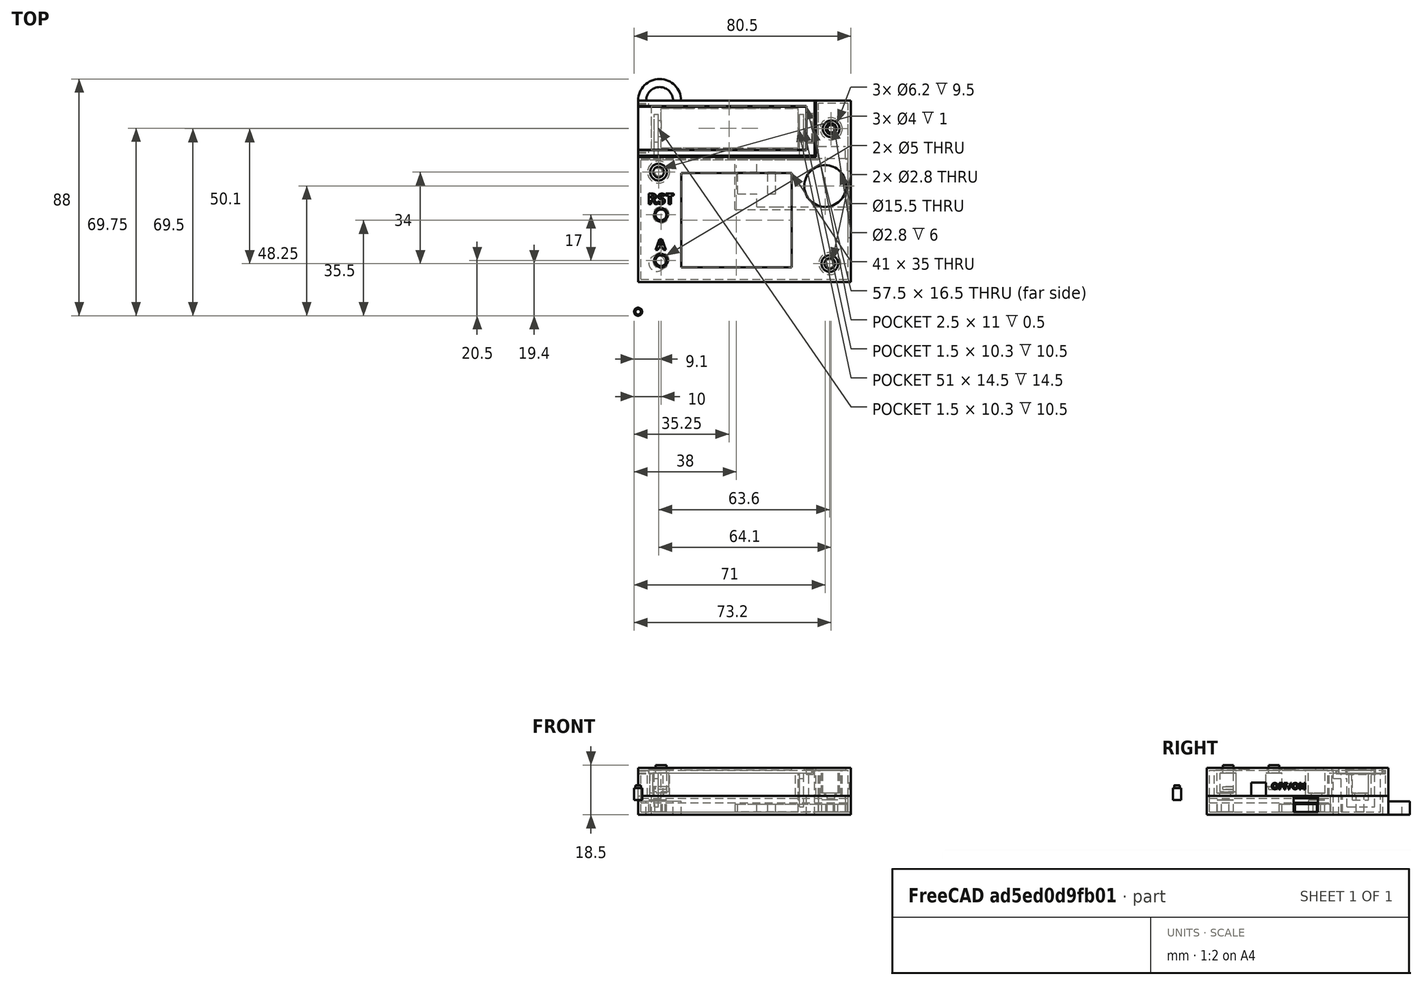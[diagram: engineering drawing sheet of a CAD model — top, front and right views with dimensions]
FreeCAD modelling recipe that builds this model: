
FCSTD DOCUMENT  (FreeCAD 0.18R16131 (Git))
Label: magic_8_power
License: All rights reserved
LicenseURL: http://en.wikipedia.org/wiki/All_rights_reserved
objects: Part::Cut×44, Part::Box×39, Part::Cylinder×28, Part::MultiFuse×10, Part::Part2DObjectPython×3, Part::Extrusion×3
note: 127 computed .brp shape members not serialized (recipe doc carries the construction recipe); baked Part::Feature solids carry a one-line shape summary decoded from their .brp

FEATURE [Part::Box] Box008  label="Cube003(usb_C_charger)"
  AttacherType = Attacher::AttachEngine3D
  Height = 3
  Length = 26.7
  Placement = pos=(27.1,-19,0) rot=(0,0,1;0rad)
  Width = 17.7
FEATURE [Part::Box] Box011  label="Cube(big_base)"
  AttacherType = Attacher::AttachEngine3D
  Height = 4
  Length = 43
  Placement = pos=(12,-20,-1) rot=(0,0,1;0rad)
  Width = 20
FEATURE [Part::Box] Box012  label="Cube(usb_c_gap)"
  AttacherType = Attacher::AttachEngine3D
  Height = 3
  Length = 3
  Placement = pos=(53.8,-14.65,0) rot=(0,0,1;0rad)
  Width = 9
FEATURE [Part::Box] Box013  label="Cube(wire_gap)"
  AttacherType = Attacher::AttachEngine3D
  Height = 3
  Length = 7
  Placement = pos=(20.1,-6.1,0) rot=(0,0,1;0rad)
  Width = 4.8
FEATURE [Part::Box] Box007  label="Cube002(DC_DC_boost)"
  AttacherType = Attacher::AttachEngine3D
  Height = 3
  Length = 11.2
  Placement = pos=(13,-14.2,0) rot=(0,0,1;0rad)
  Width = 8.1
FEATURE [Part::Box] Box014  label="Cube(wire_gap)001"
  AttacherType = Attacher::AttachEngine3D
  Height = 3
  Length = 7
  Placement = pos=(20.1,-19,0) rot=(0,0,1;0rad)
  Width = 4.8
FEATURE [Part::Cut] Cut023
  Base = -> Box011
  Tool = -> Box012
FEATURE [Part::Cut] Cut024
  Base = -> Cut023
  Tool = -> Box014
FEATURE [Part::Cut] Cut025
  Base = -> Cut024
  Tool = -> Box013
FEATURE [Part::Cut] Cut026
  Base = -> Cut025
  Tool = -> Box007
FEATURE [Part::Cut] Cut027  label="Cut027(power_board)"
  Base = -> Cut026
  Placement = pos=(24,-2,-4.5) rot=(0,0,1;0rad)
  Tool = -> Box008
FEATURE [Part::Box] Box032  label="Cube(pcb_inner)"
  AttacherType = Attacher::AttachEngine3D
  Height = 1.6
  Length = 77
  Placement = pos=(1,-48,-1) rot=(0,0,1;0rad)
  Width = 45
FEATURE [Part::Cylinder] Cylinder002  label="Cylinder(screw_left_inner)"
  Angle = 360
  AttacherType = Attacher::AttachEngine3D
  Height = 4.5
  Placement = pos=(7.6,-8.1,-4.5) rot=(0,0,1;0rad)
  Radius = 1.4
FEATURE [Part::Cylinder] Cylinder003  label="Cylinder(screw_right_inner)"
  Angle = 360
  AttacherType = Attacher::AttachEngine3D
  Height = 4.5
  Placement = pos=(71.2,-42.1,-4.5) rot=(0,0,1;0rad)
  Radius = 1.4
FEATURE [Part::Box] Box  label="Cube(inner_box)"
  AttacherType = Attacher::AttachEngine3D
  Height = 17.5
  Length = 57.5
  Placement = pos=(5,0,-5.5) rot=(0,0,1;0rad)
  Width = 16.5
FEATURE [Part::Box] Box002  label="Cube002(cover_end_gap)"
  AttacherType = Attacher::AttachEngine3D
  Height = 1.25
  Length = 4
  Placement = pos=(0,-1,9.75) rot=(0,0,1;0rad)
  Width = 18.5
FEATURE [Part::Box] Box003  label="Cube003(cover_end_top_gap)"
  AttacherType = Attacher::AttachEngine3D
  Height = 1
  Length = 5
  Placement = pos=(0,0,11) rot=(0,0,1;0rad)
  Width = 16.5
FEATURE [Part::Box] Box004  label="Cube004(lid_inner_lip)"
  AttacherType = Attacher::AttachEngine3D
  Height = 0.75
  Length = 4
  Placement = pos=(0,-0.75,10) rot=(0,0,1;0rad)
  Width = 18
FEATURE [Part::Box] Box005  label="Cube005(lid)"
  AttacherType = Attacher::AttachEngine3D
  Height = 2
  Length = 62.5
  Placement = pos=(0,0.25,10) rot=(0,0,1;0rad)
  Width = 16
FEATURE [Part::Box] Box006  label="Cube004"
  AttacherType = Attacher::AttachEngine3D
  Height = 14.5
  Length = 51
  Placement = pos=(1,1,0) rot=(0,0,1;0rad)
  Width = 14.5
FEATURE [Part::Box] Box033  label="Cube005"
  AttacherType = Attacher::AttachEngine3D
  Height = 15.5
  Length = 57.5
  Placement = pos=(-2.5,0,-1) rot=(0,0,1;0rad)
  Width = 16.5
FEATURE [Part::Box] Box034  label="Cube002(minus_spring)"
  AttacherType = Attacher::AttachEngine3D
  Height = 12.5
  Length = 1.5
  Placement = pos=(-1.5,3.1,2) rot=(0,0,1;0rad)
  Width = 10.3
FEATURE [Part::Box] Box009  label="Cube003(plus_end)"
  AttacherType = Attacher::AttachEngine3D
  Height = 12.5
  Length = 1.5
  Placement = pos=(52.5,3.1,2) rot=(0,0,1;0rad)
  Width = 10.3
FEATURE [Part::Box] Box010  label="Cube002(minus_spring_gap)"
  AttacherType = Attacher::AttachEngine3D
  Height = 10
  Length = 5
  Placement = pos=(0,5.1,4.5) rot=(0,0,1;0rad)
  Width = 6
FEATURE [Part::Box] Box035  label="Cube003(plus_end_gap)"
  AttacherType = Attacher::AttachEngine3D
  Height = 10
  Length = 5
  Placement = pos=(47.5,5.1,4.5) rot=(0,0,1;0rad)
  Width = 6
FEATURE [Part::Cut] Cut002
  Base = -> Box033
  Tool = -> Box006
FEATURE [Part::Cut] Cut003
  Base = -> Cut002
  Tool = -> Box034
FEATURE [Part::Cut] Cut004
  Base = -> Cut003
  Tool = -> Box009
FEATURE [Part::Cut] Cut005
  Base = -> Cut004
  Tool = -> Box010
FEATURE [Part::Cut] Cut006
  Base = -> Cut005
  Placement = pos=(7.5,0,-4.5) rot=(0,0,1;0rad)
  Tool = -> Box035
FEATURE [Part::Box] Box036  label="Cube006(outer_box)"
  AttacherType = Attacher::AttachEngine3D
  Height = 17.5
  Length = 60.5
  Placement = pos=(5,-2,-5.5) rot=(0,0,1;0rad)
  Width = 20.5
FEATURE [Part::Box] Box037  label="Cube007(tange_inner)"
  AttacherType = Attacher::AttachEngine3D
  Height = 1
  Length = 2
  Placement = pos=(62.5,3.25,10) rot=(0,0,1;0rad)
  Width = 10
FEATURE [Part::Box] Box038  label="Cube007(tange_outer)"
  AttacherType = Attacher::AttachEngine3D
  Height = 2
  Length = 2.5
  Placement = pos=(62.5,2.75,9.5) rot=(0,0,1;0rad)
  Width = 11
FEATURE [Part::Box] Box015  label="Cube006(under_cover_end)"
  AttacherType = Attacher::AttachEngine3D
  Height = 17.5
  Length = 5
  Placement = pos=(0,-2,-5.5) rot=(0,0,1;0rad)
  Width = 20.5
FEATURE [Part::Cut] Cut
  Base = -> Box036
  Tool = -> Box
FEATURE [Part::Cut] Cut010
  Base = -> Cut
  Tool = -> Box038
FEATURE [Part::Cut] Cut011
  Base = -> Box015
  Tool = -> Box003
FEATURE [Part::Box] Box016  label="Cube002(cover_end_gap_middle)"
  AttacherType = Attacher::AttachEngine3D
  Height = 1.25
  Length = 5
  Placement = pos=(0,0,9.75) rot=(0,0,1;0rad)
  Width = 16.5
FEATURE [Part::Cut] Cut012
  Base = -> Cut011
  Tool = -> Box016
FEATURE [Part::Cut] Cut013
  Base = -> Cut012
  Tool = -> Box002
FEATURE [Part::MultiFuse] Fusion  label="Fusion(battery_lid)"
  Shapes = -> [Box004,Box005,Box037]
FEATURE [Part::MultiFuse] Fusion001
  Shapes = -> [Cut006,Cut013,Cut010]
FEATURE [Part::Box] Box039  label="Cube(outer_case)"
  AttacherType = Attacher::AttachEngine3D
  Height = 7
  Length = 79
  Placement = pos=(0,-49,-5.5) rot=(0,0,1;0rad)
  Width = 67.5
FEATURE [Part::Cylinder] Cylinder004  label="Cylinder(screw_left_outer)"
  Angle = 360
  AttacherType = Attacher::AttachEngine3D
  Height = 4.5
  Placement = pos=(7.6,-8.1,-4.5) rot=(0,0,1;0rad)
  Radius = 3
FEATURE [Part::Cylinder] Cylinder005  label="Cylinder(screw_right_outer)"
  Angle = 360
  AttacherType = Attacher::AttachEngine3D
  Height = 4.5
  Placement = pos=(71.2,-42.1,-4.5) rot=(0,0,1;0rad)
  Radius = 3
FEATURE [Part::Box] Box040  label="Cube(gnd_wire)"
  AttacherType = Attacher::AttachEngine3D
  Height = 2
  Length = 1.5
  Placement = pos=(6,-2,8) rot=(0,0,1;0rad)
  Width = 6
FEATURE [Part::Box] Box041  label="Cube(vcc_wire)"
  AttacherType = Attacher::AttachEngine3D
  Height = 2
  Length = 1.5
  Placement = pos=(60,-2,8) rot=(0,0,1;0rad)
  Width = 6
FEATURE [Part::Box] Box042  label="Cube(switch_gap)"
  AttacherType = Attacher::AttachEngine3D
  Height = 5
  Length = 2
  Placement = pos=(78,-32.5,1.5) rot=(0,0,1;0rad)
  Width = 5.5
FEATURE [Part::Box] Box043  label="Cube(pcb_space)"
  AttacherType = Attacher::AttachEngine3D
  Height = 6
  Length = 77
  Placement = pos=(1,-48,-4.5) rot=(0,0,1;0rad)
  Width = 45
FEATURE [Part::Cylinder] Cylinder  label="Cylinder(3rd screw_inner)"
  Angle = 360
  AttacherType = Attacher::AttachEngine3D
  Height = 6
  Placement = pos=(71.7,8,-4.5) rot=(0,0,1;0rad)
  Radius = 1.4
FEATURE [Part::Box] Box044  label="Cube(battery_space)"
  AttacherType = Attacher::AttachEngine3D
  Height = 17.5
  Length = 57.5
  Placement = pos=(5,0,-5.5) rot=(0,0,1;0rad)
  Width = 16.5
FEATURE [Part::Box] Box046  label="Cube(mirco_usb_port)"
  AttacherType = Attacher::AttachEngine3D
  Height = 6
  Length = 1.2
  Placement = pos=(77.8,-16.65,-4.5) rot=(0,0,1;0rad)
  Width = 9
FEATURE [Part::Box] Box047  label="Cube(outer_lid)"
  AttacherType = Attacher::AttachEngine3D
  Height = 10.5
  Length = 79
  Placement = pos=(0,-49,1.5) rot=(0,0,1;0rad)
  Width = 46.5
FEATURE [Part::Box] Box048  label="Cube(inner_lid)"
  AttacherType = Attacher::AttachEngine3D
  Height = 9.5
  Length = 77
  Placement = pos=(1,-48,1.5) rot=(0,0,1;0rad)
  Width = 44.5
FEATURE [Part::Box] Box049  label="Cube(3rd_screw_cover_outer)"
  AttacherType = Attacher::AttachEngine3D
  Height = 10.5
  Length = 13
  Placement = pos=(66,-2.5,1.5) rot=(0,0,1;0rad)
  Width = 21
FEATURE [Part::Cylinder] Cylinder006  label="Cylinder(3rd screw_lid_clear)"
  Angle = 360
  AttacherType = Attacher::AttachEngine3D
  Height = 10.5
  Placement = pos=(71.7,8,0.5) rot=(0,0,1;0rad)
  Radius = 2
FEATURE [Part::Cylinder] Cylinder007  label="Cylinder(3rd screw_lid_head_clear_inner)"
  Angle = 360
  AttacherType = Attacher::AttachEngine3D
  Height = 9.5
  Placement = pos=(71.7,8,2.5) rot=(0,0,1;0rad)
  Radius = 3.1
FEATURE [Part::Box] Box050  label="Cube(3rd_screw_cover_inner)"
  AttacherType = Attacher::AttachEngine3D
  Height = 10.5
  Length = 11
  Placement = pos=(67,-3.5,0.5) rot=(0,0,1;0rad)
  Width = 21
FEATURE [Part::Cylinder] Cylinder008  label="Cylinder(3rd screw_lid_head_clear_outer)"
  Angle = 360
  AttacherType = Attacher::AttachEngine3D
  Height = 10.5
  Placement = pos=(71.7,8,1.5) rot=(0,0,1;0rad)
  Radius = 4.1
FEATURE [Part::Cut] Cut030
  Base = -> Fusion001
  Tool = -> Box040
FEATURE [Part::Cut] Cut031  label="Cut031(battery)"
  Base = -> Cut030
  Tool = -> Box041
FEATURE [Part::Cylinder] Cylinder009  label="Cylinder(gx-12_hole)"
  Angle = 360
  AttacherType = Attacher::AttachEngine3D
  Height = 10
  Placement = pos=(69.5,-13.25,3) rot=(0,0,1;0rad)
  Radius = 7.75
FEATURE [Part::Box] Box051  label="Cube(screen_cutout)"
  AttacherType = Attacher::AttachEngine3D
  Height = 10
  Length = 41
  Placement = pos=(16,-43.5,3) rot=(0,0,1;0rad)
  Width = 35
FEATURE [Part::Cut] Cut032
  Base = -> Box039
  Tool = -> Box043
FEATURE [Part::Cut] Cut033
  Base = -> Cut032
  Tool = -> Box044
FEATURE [Part::Cut] Cut034
  Base = -> Cut033
  Tool = -> Cylinder
FEATURE [Part::Cut] Cut037
  Base = -> Cut034
  Tool = -> Box046
FEATURE [Part::Cylinder] Cylinder011  label="Cylinder(under_button_post)"
  Angle = 360
  AttacherType = Attacher::AttachEngine3D
  Height = 4.5
  Placement = pos=(7,-42,-4.5) rot=(0,0,1;0rad)
  Radius = 3
FEATURE [Part::Cylinder] Cylinder012  label="Cylinder(lanyard_outer)"
  Angle = 360
  AttacherType = Attacher::AttachEngine3D
  Height = 5
  Placement = pos=(8,18.5,-5.5) rot=(0,0,1;0rad)
  Radius = 8
FEATURE [Part::Cylinder] Cylinder013  label="Cylinder(lanyard_inner)"
  Angle = 360
  AttacherType = Attacher::AttachEngine3D
  Height = 5
  Placement = pos=(8,18.5,-5.5) rot=(0,0,1;0rad)
  Radius = 5
FEATURE [Part::Box] Box052  label="Cube(lanyard_cut)"
  AttacherType = Attacher::AttachEngine3D
  Height = 10
  Length = 16
  Placement = pos=(0,8.5,-5.5) rot=(0,0,1;0rad)
  Width = 10
FEATURE [Part::Cut] Cut038
  Base = -> Cylinder012
  Tool = -> Cylinder013
FEATURE [Part::Cut] Cut039  label="Cut039(lanyard)"
  Base = -> Cut038
  Tool = -> Box052
FEATURE [Part::Box] Box053  label="Cube(cable_gap)"
  AttacherType = Attacher::AttachEngine3D
  Height = 6
  Length = 10
  Placement = pos=(67,-3.5,-4.5) rot=(0,0,1;0rad)
  Width = 5
FEATURE [Part::MultiFuse] Fusion002
  Shapes = -> [Cut037,Cut027]
FEATURE [Part::Cut] Cut040
  Base = -> Fusion002
  Tool = -> Box053
FEATURE [Part::Cylinder] Cylinder014  label="Cylinder(screw_left_lid_clear)"
  Angle = 360
  AttacherType = Attacher::AttachEngine3D
  Height = 10.5
  Placement = pos=(7.6,-8.1,0.5) rot=(0,0,1;0rad)
  Radius = 2
FEATURE [Part::Cylinder] Cylinder015  label="Cylinder(screw_left_head_clear_inner)"
  Angle = 360
  AttacherType = Attacher::AttachEngine3D
  Height = 9.5
  Placement = pos=(7.6,-8.1,2.5) rot=(0,0,1;0rad)
  Radius = 3.1
FEATURE [Part::Cylinder] Cylinder016  label="Cylinder(screw_left_head_clear_outer)"
  Angle = 360
  AttacherType = Attacher::AttachEngine3D
  Height = 10.5
  Placement = pos=(7.6,-8.1,1.5) rot=(0,0,1;0rad)
  Radius = 4.1
FEATURE [Part::Cut] Cut041
  Base = -> Cylinder004
  Tool = -> Cylinder002
FEATURE [Part::Cylinder] Cylinder017  label="Cylinder(screw_right_lid_clear)"
  Angle = 360
  AttacherType = Attacher::AttachEngine3D
  Height = 10.5
  Placement = pos=(71.2,-42.1,0.5) rot=(0,0,1;0rad)
  Radius = 2
FEATURE [Part::Cut] Cut042
  Base = -> Cylinder005
  Tool = -> Cylinder003
FEATURE [Part::Cylinder] Cylinder018  label="Cylinder(screw_right_head_clear_inner)"
  Angle = 360
  AttacherType = Attacher::AttachEngine3D
  Height = 9.5
  Placement = pos=(71.2,-42.1,2.5) rot=(0,0,1;0rad)
  Radius = 3.1
FEATURE [Part::Cylinder] Cylinder019  label="Cylinder(screw_right_head_clear_outer)"
  Angle = 360
  AttacherType = Attacher::AttachEngine3D
  Height = 10.5
  Placement = pos=(71.2,-42.1,1.5) rot=(0,0,1;0rad)
  Radius = 4.1
FEATURE [Part::Box] Box054  label="Cube(GND_wire_cover_hole)"
  AttacherType = Attacher::AttachEngine3D
  Height = 8.5
  Length = 5
  Placement = pos=(4.3,-3.5,1.5) rot=(0,0,1;0rad)
  Width = 1
FEATURE [Part::Box] Box055  label="Cube(VCC_wire_cover_hole)"
  AttacherType = Attacher::AttachEngine3D
  Height = 8.5
  Length = 5
  Placement = pos=(58.4,-3.5,1.5) rot=(0,0,1;0rad)
  Width = 1
FEATURE [Part::Cylinder] Cylinder020  label="Cylinder(reset_button_hole)"
  Angle = 360
  AttacherType = Attacher::AttachEngine3D
  Height = 10
  Placement = pos=(8.5,-24,3) rot=(0,0,1;0rad)
  Radius = 2.5
FEATURE [Part::Cylinder] Cylinder021  label="Cylinder(a_button_hole)"
  Angle = 360
  AttacherType = Attacher::AttachEngine3D
  Height = 10
  Placement = pos=(8.5,-41,3) rot=(0,0,1;0rad)
  Radius = 2.5
FEATURE [Part::MultiFuse] Fusion003
  Shapes = -> [Box047,Box049]
FEATURE [Part::Cut] Cut043
  Base = -> Fusion003
  Tool = -> Box048
FEATURE [Part::Cut] Cut044
  Base = -> Cut043
  Tool = -> Box050
FEATURE [Part::Cut] Cut045
  Base = -> Cut044
  Tool = -> Box055
FEATURE [Part::Cut] Cut046
  Base = -> Cut045
  Tool = -> Box054
FEATURE [Part::MultiFuse] Fusion004
  Shapes = -> [Cylinder019,Cut046]
FEATURE [Part::MultiFuse] Fusion005
  Shapes = -> [Fusion004,Cylinder016]
FEATURE [Part::Cut] Cut047
  Base = -> Fusion005
  Tool = -> Cylinder018
FEATURE [Part::Cut] Cut048
  Base = -> Cut047
  Tool = -> Cylinder017
FEATURE [Part::Cut] Cut049
  Base = -> Cut048
  Tool = -> Cylinder014
FEATURE [Part::Cut] Cut050
  Base = -> Cut049
  Tool = -> Cylinder015
FEATURE [Part::Cut] Cut051
  Base = -> Cut050
  Tool = -> Cylinder021
FEATURE [Part::Cut] Cut052
  Base = -> Cut051
  Tool = -> Cylinder020
FEATURE [Part::Cut] Cut053
  Base = -> Cut052
  Tool = -> Box051
FEATURE [Part::Cut] Cut054
  Base = -> Cut053
  Tool = -> Cylinder009
FEATURE [Part::MultiFuse] Fusion006
  Shapes = -> [Cut054,Cylinder008]
FEATURE [Part::Cut] Cut055
  Base = -> Fusion006
  Tool = -> Cylinder006
FEATURE [Part::Cut] Cut056
  Base = -> Cut055
  Tool = -> Cylinder007
FEATURE [Part::Cut] Cut057
  Base = -> Cut056
  Tool = -> Box042
FEATURE [Part::Part2DObjectPython] ShapeString  # Draft 2D object (typed FeaturePython)
  FontFile = <userpath>/A6E4-ED97/3dprinting/fonts/open-sans/OpenSans-Bold.ttf
  Placement = pos=(3.5,-20,12) rot=(0,0,1;0rad)
  Size = 5
  String = RST
  Tracking = 0
FEATURE [Part::Part2DObjectPython] ShapeString001  # Draft 2D object (typed FeaturePython)
  FontFile = <userpath>/A6E4-ED97/3dprinting/fonts/open-sans/OpenSans-Bold.ttf
  Placement = pos=(6.5,-37,12) rot=(0,0,1;0rad)
  Size = 5
  String = A
  Tracking = 0
FEATURE [Part::Part2DObjectPython] ShapeString002  # Draft 2D object (typed FeaturePython)
  FontFile = <userpath>/A6E4-ED97/3dprinting/fonts/open-sans/OpenSans-Bold.ttf
  Placement = pos=(80,-25,4) rot=(0.57735,0.57735,0.57735;2.0944rad)
  Size = 3
  String = OFF/ON
  Tracking = 0
FEATURE [Part::Extrusion] Extrude
  Base = -> ShapeString002
  Dir = (1,-1e-16,2e-16)
  DirMode = 2
  FaceMakerClass = Part::FaceMakerBullseye
  LengthFwd = 1
  LengthRev = 0
  Placement = pos=(-1.5,0,0) rot=(0,0,1;0rad)
  Solid = false
  Symmetric = false
FEATURE [Part::Extrusion] Extrude001
  Base = -> ShapeString
  Dir = (0,0,1)
  DirMode = 2
  FaceMakerClass = Part::FaceMakerBullseye
  LengthFwd = 1
  LengthRev = 0
  Placement = pos=(0,0,-0.5) rot=(0,0,1;0rad)
  Solid = false
  Symmetric = false
FEATURE [Part::Extrusion] Extrude002
  Base = -> ShapeString001
  Dir = (0,0,1)
  DirMode = 2
  FaceMakerClass = Part::FaceMakerBullseye
  LengthFwd = 1
  LengthRev = 0
  Placement = pos=(0,0,-0.5) rot=(0,0,1;0rad)
  Solid = false
  Symmetric = false
FEATURE [Part::Cut] Cut058
  Base = -> Cut057
  Tool = -> Extrude
FEATURE [Part::Cut] Cut059
  Base = -> Cut058
  Tool = -> Extrude002
FEATURE [Part::Cut] Cut060
  Base = -> Cut059
  Tool = -> Extrude001
FEATURE [Part::Cylinder] Cylinder022  label="Cylinder(rst_buttom_bottom)"
  Angle = 360
  AttacherType = Attacher::AttachEngine3D
  Height = 5
  Placement = pos=(8.5,-24,5) rot=(0,0,1;0rad)
  Radius = 3
FEATURE [Part::Cylinder] Cylinder024  label="Cylinder(rst_buttom_bottom_cutout)"
  Angle = 360
  AttacherType = Attacher::AttachEngine3D
  Height = 1
  Placement = pos=(8.5,-24,4) rot=(0,0,1;0rad)
  Radius = 2
FEATURE [Part::Cylinder] Cylinder023  label="Cylinder(rst_buttom_top)"
  Angle = 360
  AttacherType = Attacher::AttachEngine3D
  Height = 3
  Placement = pos=(8.5,-24,10) rot=(0,0,1;0rad)
  Radius = 2
FEATURE [Part::Cylinder] Cylinder025  label="Cylinder(a_buttom_top)"
  Angle = 360
  AttacherType = Attacher::AttachEngine3D
  Height = 3
  Placement = pos=(8.5,-41,10) rot=(0,0,1;0rad)
  Radius = 2
FEATURE [Part::Cylinder] Cylinder026  label="Cylinder(a_buttom_bottom)"
  Angle = 360
  AttacherType = Attacher::AttachEngine3D
  Height = 7
  Placement = pos=(8.5,-41,3) rot=(0,0,1;0rad)
  Radius = 3
FEATURE [Part::Cylinder] Cylinder027  label="Cylinder(a_buttom_bottom_cutout)"
  Angle = 360
  AttacherType = Attacher::AttachEngine3D
  Height = 1
  Placement = pos=(8.5,-41,4) rot=(0,0,1;0rad)
  Radius = 2
FEATURE [Part::MultiFuse] Fusion007
  Shapes = -> [Cylinder022,Cylinder023]
FEATURE [Part::Cylinder] Cylinder028  label="Cylinder(screen_support_bottom)"
  Angle = 360
  AttacherType = Attacher::AttachEngine3D
  Height = 4.5
  Placement = pos=(0,-60,0) rot=(0,0,1;0rad)
  Radius = 1.5
FEATURE [Part::MultiFuse] Fusion008
  Shapes = -> [Cylinder025,Cylinder026]
FEATURE [Part::Cylinder] Cylinder029  label="Cylinder(screen_support_top)"
  Angle = 360
  AttacherType = Attacher::AttachEngine3D
  Height = 1
  Placement = pos=(0,-60,4.5) rot=(0,0,1;0rad)
  Radius = 1
FEATURE [Part::MultiFuse] Fusion009
  Shapes = -> [Cylinder028,Cylinder029]
